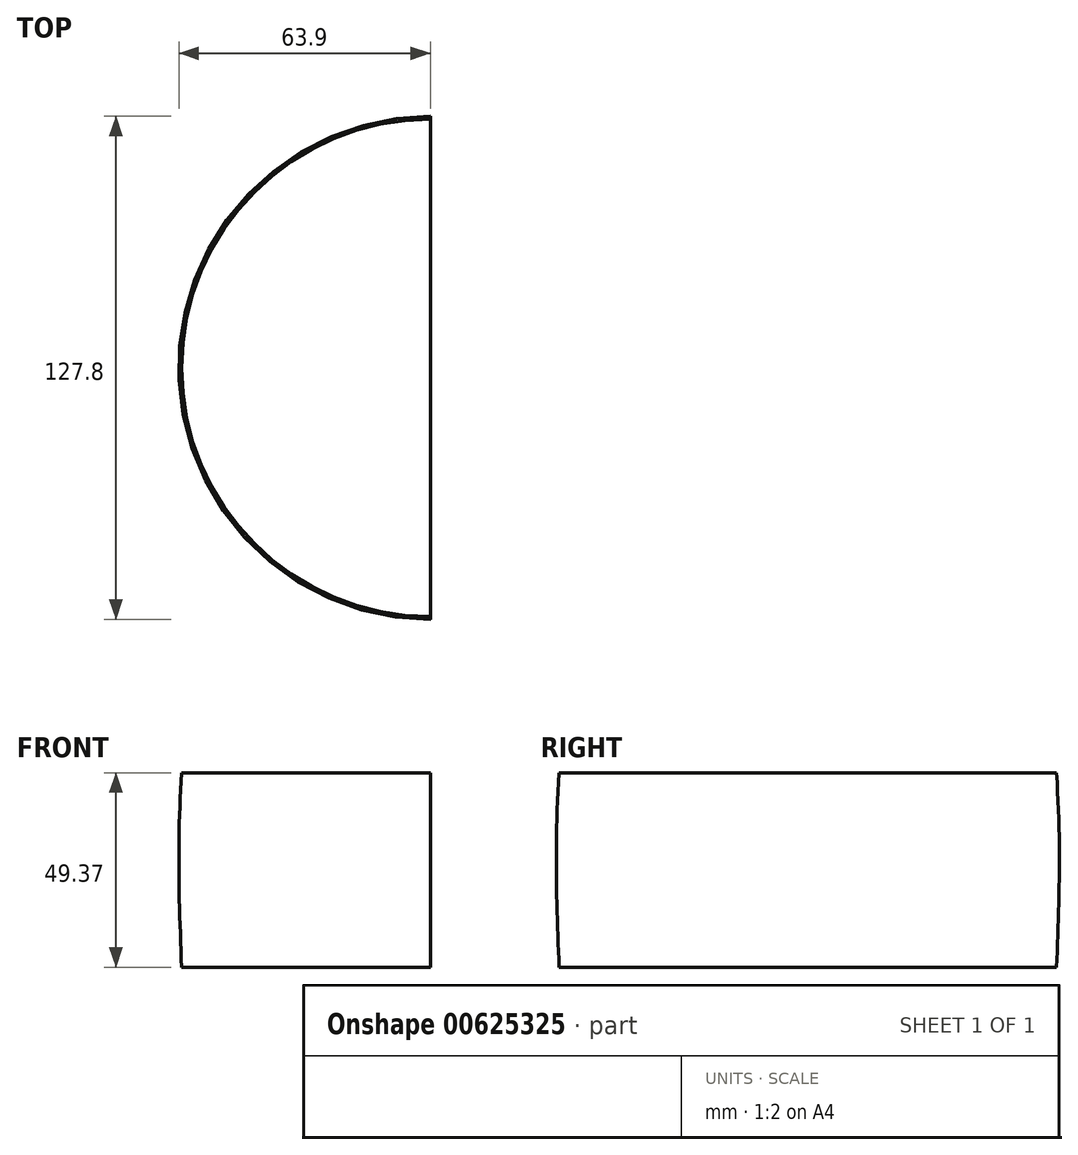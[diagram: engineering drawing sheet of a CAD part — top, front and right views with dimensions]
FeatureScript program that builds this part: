
annotation { "Feature Type Name" : "Feature", "Feature Type Description" : "" }
export const myFeature = defineFeature(function(context is Context, id is Id, definition is map)
    precondition{}
    {
        {
            var Q0;
            Q0=qCreatedBy(makeId("Right.planeOp"),FACE);
            var sketch = newSketch(context, id + "F0", { "sketchPlane" : qUnion([Q0])});
            skLineSegment(sketch, "E0", {"start": v(-36.24, -36.42) * mm, "end": v(37.5, -36.42) * mm});
            skLineSegment(sketch, "E1", {"start": v(-36.24, -36.42) * mm, "end": v(-36.24, 141.08) * mm});
            skLineSegment(sketch, "E2", {"start": v(-36.24, 85.74) * mm, "end": v(9.92, 85.74) * mm});
            skLineSegment(sketch, "E3", {"start": v(-36.24, 12.95) * mm, "end": v(26.94, 12.95) * mm});
            skFitSpline(sketch, "E4", {"points": [v(-36.24, 141.08) * mm, v(9.92, 85.74) * mm, v(26.94, 12.95) * mm, v(26.94, -36.42) * mm], "startDerivative": vector(150.2, -142.81) * mm, "endDerivative": vector(-6.37, -158.87) * mm});
            skSolve(sketch);
        }
        {
            var Q0;
            {var subQ5=sQuery(id+"F0.wireOp",EDGE,"E3");Q0=makeQuery(id+"F0.imprint","IMPRINT",FACE,{"disambiguationData":[TD([[makeQuery(id+"F0.imprint","IMPRINT",EDGE,{"derivedFrom":subQ5}),-1.0]])]});}
            var Q1;
            Q1=sQuery(id+"F0.wireOp",EDGE,"E1");
            revolve(context, id + "F1", {"entities" : qUnion([Q0]), "axis" : qUnion([Q1]), "revolveType" : RevolveType.ONE_DIRECTION, "angle" : 180 * degree});
        }
    });
